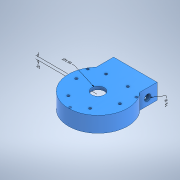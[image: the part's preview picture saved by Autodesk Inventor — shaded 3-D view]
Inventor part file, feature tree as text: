
AUTODESK INVENTOR PART (.ipt)
format: ipt  version: 2022.2 (Build 262287000, 287)  size: 697,856 bytes
history: native  units: in
note: dims shown in document units (in); Inventor stores cm internally (conversion verified against a paired STEP export)
features: sketch x8, other x7, extrude x7, reference x6, thicken_offset x3, hole x2, mirror x1, emboss x1
ambient origin geometry x8: Origin, YZ Plane, XZ Plane, XY Plane, X Axis, Y Axis, Z Axis, Center Point
bodies: Solid1 (feature_tree)
feature tree (35):
  other  "Annotations"
  extrude  "Extrusion1"  Depth=0.25in TaperAngle=0.0deg
  sketch  "Sketch3"  dims[d0=4.25in d1=0.25in d2=0.0in]
  extrude  "Extrusion3"  Depth=1.5in
  extrude  "Extrusion4"  Depth=0.25in
  extrude  "Extrusion6"  Depth=0.25in
  extrude  "Extrusion7"  Depth=0.25in TaperAngle=0.0deg
  thicken_offset  "Thicken1"
  thicken_offset  "Thicken2"
  mirror  "Mirror2"
  thicken_offset  "Thicken3"
  extrude  "Extrusion11"  Depth=0.375in
  hole  "Hole4"  [1 undecoded]
  extrude  "Extrusion13"  Depth=0.005in
  hole  "Hole5"  [1 undecoded]
  emboss  "Emboss1"
  sketch  "Sketch4"  dims[d6=2.75in d7=1.5in]
  reference  "Reference1"
  reference  "Reference2"
  reference  "Reference3"
  reference  "Reference4"
  reference  "Reference5"
  reference  "Reference6"
  sketch  "Sketch5"  dims[d8=0.25in d9=0.25in]
  sketch  "Sketch9"  dims[d10=0.25in d11=0.25in]
  sketch  "Sketch12"  dims[d12=1.0in d13=0.0in d14=0.25in d15=0.0in]
  sketch  "Sketch14"  dims[d20=0.5in d21=0.375in]
  sketch  "Sketch15"  dims[d22=0.0in d23=0.0in d24=1.0in]
  sketch  "Sketch16"  dims[d25=0.0in d26=0.0in d27=0.005in d28=0.005in d29=0.005in d30=0.005in d31=0.005in d32=0.005in d47=3.75in d50=0.25in d51=0.0in d78=1.75in d79=2.3622in d81=360.0deg d83=0.201in d84=0.75in d85=0.4in d86=0.125in d87=0.5635in d88=1.0in d89=0.8108in d96=0.55in d97=1.0in d98=0.0in d99=2.3622in d101=360.0deg d104=0.125in d105=0.125in d106=0.0in d107=1.1811in d109=360.0deg d111=0.185in d112=0.75in d113=0.2173in d114=0.2186in d115=0.5635in d116=1.0in d117=0.8108in d118=2.25in d119=0.1in d120=0.0in d103=0.25in d40=2.3981in d41=1.01in d52=1.4746in d53=0.51in d54=0.5in d55=0.0344in]
  other  "forkMountForDecTripV03.iam"
  other  "Worm Gears:2"
  other  "Worm:1"
  other  "Diameter Dimension 1"
  other  "Diameter Dimension 2"
  other  "Linear Dimension 1"
note: 2 required parameter values undecoded (feature->parameter linkage not recoverable at this tier; creation-order binding heuristic only, values carry confidence <= 0.55)
